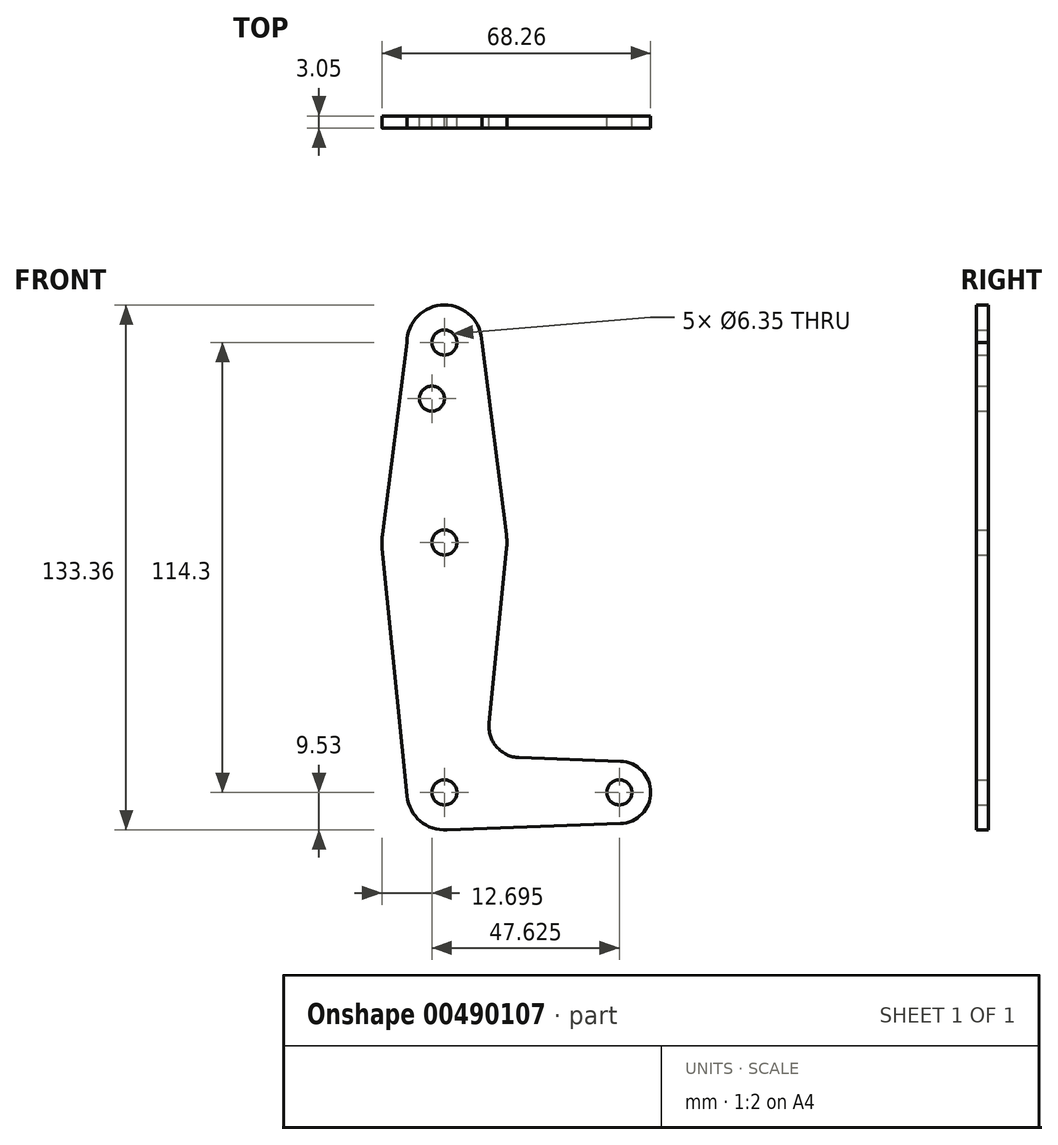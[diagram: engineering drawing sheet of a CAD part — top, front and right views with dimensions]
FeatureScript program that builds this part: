
annotation { "Feature Type Name" : "Feature", "Feature Type Description" : "" }
export const myFeature = defineFeature(function(context is Context, id is Id, definition is map)
    precondition{}
    {
        {
            var Q0;
            Q0=qCreatedBy(makeId("Front.planeOp"),FACE);
            var sketch = newSketch(context, id + "F0", { "sketchPlane" : qUnion([Q0])});
            skLineSegment(sketch, "E0", {"start": v(0, 0) * mm, "end": v(0, 114.3) * mm, "construction": true});
            skCircle(sketch, "E1", {"center": v(0, 114.3) * mm, "radius": 9.53 * mm});
            skCircle(sketch, "E2", {"center": v(0, 63.5) * mm, "radius": 15.88 * mm});
            skCircle(sketch, "E3", {"center": v(0, 0) * mm, "radius": 9.53 * mm});
            skLineSegment(sketch, "E4", {"start": v(-9.53, 114.3) * mm, "end": v(-15.75, 65.5) * mm});
            skLineSegment(sketch, "E5", {"start": v(9.53, 114.3) * mm, "end": v(15.75, 65.5) * mm});
            skLineSegment(sketch, "E6", {"start": v(0, 0) * mm, "end": v(44.45, 0) * mm});
            skCircle(sketch, "E7", {"center": v(44.45, 0) * mm, "radius": 7.94 * mm});
            skLineSegment(sketch, "E8", {"start": v(-15.8, 61.91) * mm, "end": v(-9.48, -0.95) * mm});
            skLineSegment(sketch, "E9", {"start": v(11.34, 17.59) * mm, "end": v(15.8, 61.91) * mm});
            skLineSegment(sketch, "E10", {"start": v(18.97, 8.85) * mm, "end": v(44.73, 7.93) * mm});
            skLineSegment(sketch, "E11", {"start": v(0, -9.53) * mm, "end": v(44.73, -7.93) * mm});
            skCircle(sketch, "E12", {"center": v(0, 114.3) * mm, "radius": 3.18 * mm});
            skCircle(sketch, "E13", {"center": v(0, 63.5) * mm, "radius": 3.18 * mm});
            skCircle(sketch, "E14", {"center": v(0, 0) * mm, "radius": 3.18 * mm});
            skCircle(sketch, "E15", {"center": v(44.45, 0) * mm, "radius": 3.18 * mm});
            skCircle(sketch, "E16", {"center": v(-3.18, 100.03) * mm, "radius": 3.18 * mm});
            skArc(sketch, "E17.filletArc", {"start": v(11.34, 17.59) * mm, "mid": v(13.26, 11.57) * mm, "end": v(18.97, 8.85) * mm});
            skSolve(sketch);
        }
        {
            var Q0;
            Q0 = qSketchRegion(id + "F0", true);
            extrude(context, id + "F1", {"entities" : qUnion([Q0]), "depth" : 3.05 * mm});
        }
    });
